# Revit family: DBLTD_TheSenatorGroup_Whiteboards_Colab
name_source: partatom
category: Furniture
units: mm (PartAtom-declared; Revit-internal decimal feet)

## family parameters
Always vertical = Yes
Cut with Voids When Loaded = No
OmniClass Number = 23.40.20.00
OmniClass Title = General Furniture and Specialties
Room Calculation Point = No
Shared = Yes
Work Plane-Based = No

## types (12) — shared parameters
Assembly Code = E2020200
AssetType = Movable
Category = Pr_40_30_25_96  Whiteboards
Color = Legs; Honey Yellow | Forest Green | Smoke Grey | Ocean Blue. Frame; Smoke Grey. Fabric: Blazer
Constituents = Legs, Frame and Board
DurationUnit = years
ExpectedLife = 5
Finish = Legs; Honey Yellow | Forest Green | Smoke Grey | Ocean Blue. Frame; Smoke Grey. Fabric: Blazer
Keynote = Pr_40_30_25_96  Whiteboards
Manufacturer = The Senator Group
ManufacturerName = The Senator Group
ManufacturerURL = https://www.thesenatorgroup.com
Name = Whiteboards
NominalDepth = 650 mm  [stored 2.13255 ft]
NominalHeight = 1850 mm  [stored 6.06955 ft]
ProductInformation = https://www.senator.online
Shape = Rectangular
URL = https://www.thesenatorgroup.com
Uniclass2015Code = Pr_40_30_25_96
Uniclass2015Title = Whiteboards
Uniclass2015Version = Products v1.32
Version = 1
WarrantyDescription = The Senator Group warrants that its manufactured products are free from manufacturing defects - in materials or workmanship - for a period of five (5) years.
WarrantyDurationLabor = 5
WarrantyDurationParts = 5
WarrantyDurationUnit = years
WarrantyGuarantorLabor = https://www.thesenatorgroup.com
WarrantyGuarantorParts = https://www.thesenatorgroup.com
zero-valued in all types: Cost, Default Elevation

## per-type parameters (varying)
| type | Material | MediaPlaceHolder | Model | ModelNumber | NominalWidth | Size |
| 1250mm Drywipe | Legs and Frame; Steel. Board; Drywipe | No | CB2012D | CB2012D | 1250 mm  [stored 4.10105 ft] | 1850 x 1250 x 650 mm |
| 1650mm Drywipe | Legs and Frame; Steel. Board; Drywipe | No | CB2016D | CB2016D | 1650 mm  [stored 5.41339 ft] | 1850 x 1650 x 650 mm |
| 1650mm Pinboard | Legs and Frame; Steel. Board; Pinboard | No | CB2016P | CB2016P | 1650 mm  [stored 5.41339 ft] | 1850 x 1650 x 650 mm |
| 1250mm Pinboard | Legs and Frame; Steel. Board; Pinboard | No | CB2012P | CB2012P | 1250 mm  [stored 4.10105 ft] | 1850 x 1250 x 650 mm |
| 1250mm Magic Drywipe | Legs and Frame; Steel. Board; Magic Drywipe | No | CB2012MD | CB2012MD | 1250 mm  [stored 4.10105 ft] | 1850 x 1250 x 650 mm |
| 1650mm Magic Drywipe | Legs and Frame; Steel. Board; Magic Drywipe | No | CB2016MD | CB2016MD | 1650 mm  [stored 5.41339 ft] | 1850 x 1650 x 650 mm |
| 1250mm Drywipe & Pinboard | Legs and Frame; Steel. Board; Drywipe & Pinboard | No | CB2012DP | CB2012DP | 1250 mm  [stored 4.10105 ft] | 1850 x 1250 x 650 mm |
| 1250mm Magic Drywipe & Pinboard | Legs and Frame; Steel. Board; Magic Drywipe & Pinboard | No | CB2012MDP | CB2012MDP | 1250 mm  [stored 4.10105 ft] | 1850 x 1250 x 650 mm |
| 1650mm Drywipe & Pinboard | Legs and Frame; Steel. Board; Drywipe & Pinboard | No | CB2016DP | CB2016DP | 1650 mm  [stored 5.41339 ft] | 1850 x 1650 x 650 mm |
| 1650mm Magic Drywipe & Pinboard | Legs and Frame; Steel. Board; Magic Drywipe & Pinboard | No | CB2016MDP | CB2016MDP | 1650 mm  [stored 5.41339 ft] | 1850 x 1650 x 650 mm |
| 1650mm Media & Pinboard | Legs and Frame; Steel. Board; Media  & Pinboard | Yes | CB2016PM | CB2016PM | 1650 mm  [stored 5.41339 ft] | 1850 x 1650 x 650 mm |
| 1250mm Media & Pinboard | Legs and Frame; Steel. Board; Media  & Pinboard | Yes | CB2012PM | CB2012PM | 1250 mm  [stored 4.10105 ft] | 1850 x 1250 x 650 mm |

note: column(s) folded — value = type name in every type: Description, ModelReference, Type Comments

note: [stored X ft] marks values corroborated as IEEE doubles in the binary element streams (Revit-internal decimal feet)

## geometry (parser evidence)
native form markers: Sweep x6
no freeform markers — native parametric forms only
